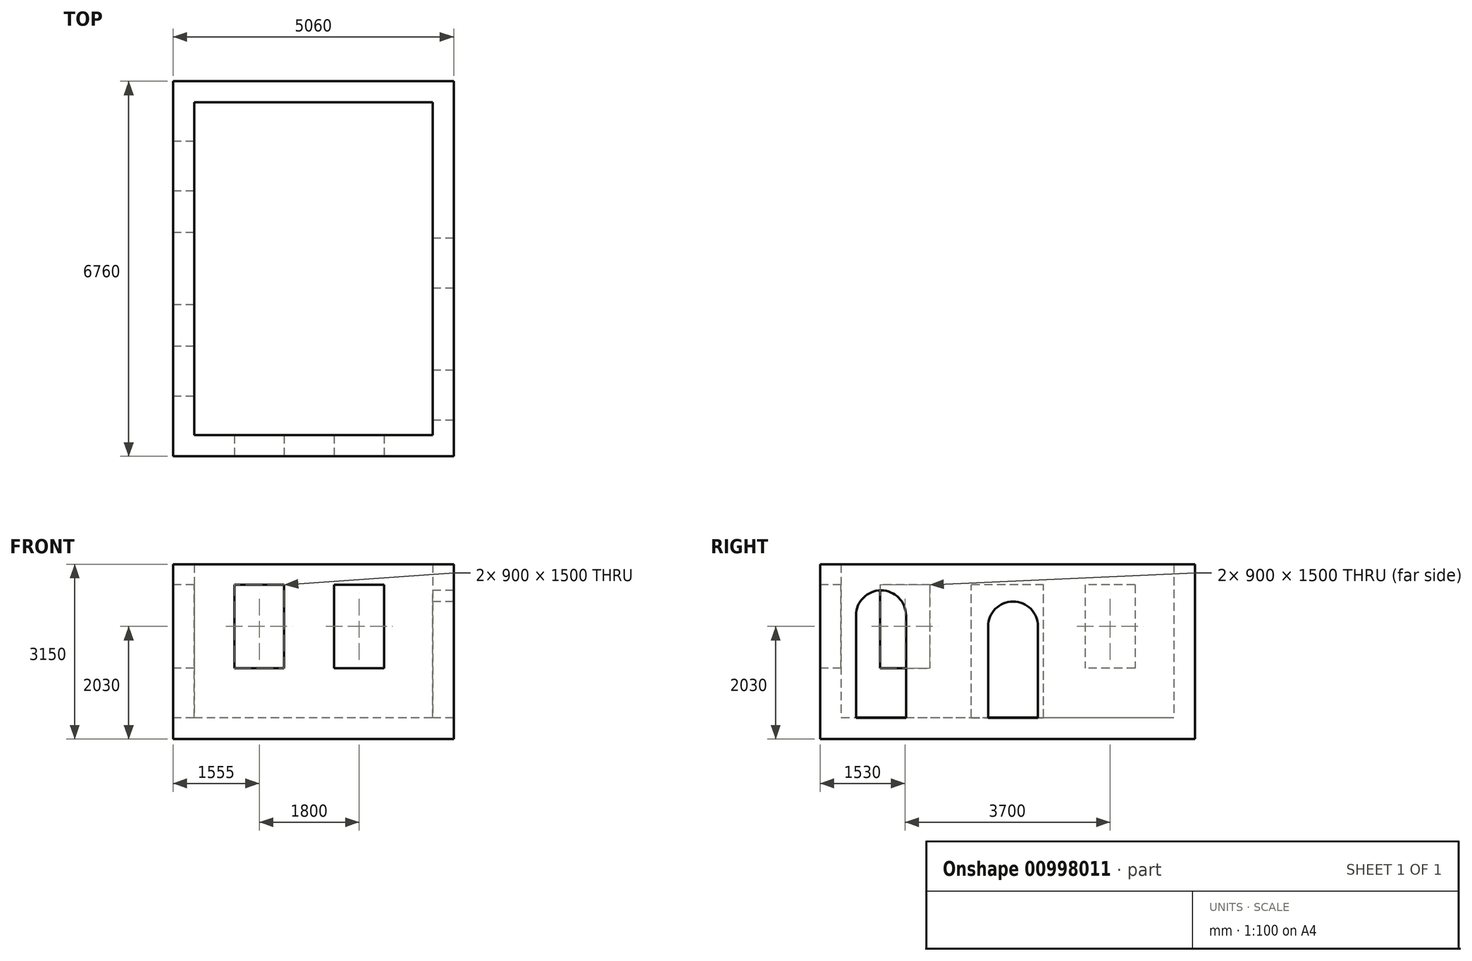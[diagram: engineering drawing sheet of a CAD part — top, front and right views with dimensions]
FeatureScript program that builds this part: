
annotation { "Feature Type Name" : "Feature", "Feature Type Description" : "" }
export const myFeature = defineFeature(function(context is Context, id is Id, definition is map)
    precondition{}
    {
        {
            var Q0;
            Q0=qCreatedBy(makeId("Top.planeOp"),FACE);
            var sketch = newSketch(context, id + "F0", { "sketchPlane" : qUnion([Q0])});
            skLineSegment(sketch, "E0.bottom", {"start": v(-2530, -3380) * mm, "end": v(2530, -3380) * mm});
            skLineSegment(sketch, "E0.top", {"start": v(-2530, 3380) * mm, "end": v(2530, 3380) * mm});
            skLineSegment(sketch, "E0.left", {"start": v(-2530, -3380) * mm, "end": v(-2530, 3380) * mm});
            skLineSegment(sketch, "E0.right", {"start": v(2530, -3380) * mm, "end": v(2530, 3380) * mm});
            skLineSegment(sketch, "E1", {"start": v(0, 0) * mm, "end": v(0, -4189.53) * mm, "construction": true});
            skLineSegment(sketch, "E2", {"start": v(59.84, 0) * mm, "end": v(5067.34, 0) * mm, "construction": true});
            skSolve(sketch);
        }
        {
            var Q0;
            Q0 = qSketchRegion(id + "F0", true);
            extrude(context, id + "F1", {"entities" : qUnion([Q0]), "depth" : (2750 + 400) * mm, "offsetDistance" : 25 * mm});
        }
        {
            var Q0;
            Q0=makeQuery(id+"F1.opExtrude","CAP_FACE",FACE,{"disambiguationData":[OSD([sQuery(id+"F0.wireOp",EDGE,"E0.bottom"),sQuery(id+"F0.wireOp",EDGE,"E0.top"),sQuery(id+"F0.wireOp",EDGE,"E0.left"),sQuery(id+"F0.wireOp",EDGE,"E0.right")])],"isStart":false});
            shell(context, id + "F2", {"entities" : qUnion([Q0]), "thickness" : 380 * mm});
        }
        {
            var Q0;
            Q0=makeQuery(id+"F1.opExtrude","SWEPT_FACE",FACE,{"disambiguationData":[OSD([sQuery(id+"F0.wireOp",EDGE,"E0.left")])]});
            var sketch = newSketch(context, id + "F3", { "sketchPlane" : qUnion([Q0])});
            skLineSegment(sketch, "E3.bottom", {"start": v(-650, 380) * mm, "end": v(650, 380) * mm});
            skLineSegment(sketch, "E3.top", {"start": v(-650, 2780) * mm, "end": v(650, 2780) * mm});
            skLineSegment(sketch, "E3.left", {"start": v(-650, 380) * mm, "end": v(-650, 2780) * mm});
            skLineSegment(sketch, "E3.right", {"start": v(650, 380) * mm, "end": v(650, 2780) * mm});
            skLineSegment(sketch, "E4", {"start": v(0, 2780) * mm, "end": v(0, 380) * mm, "construction": true});
            skLineSegment(sketch, "E5.bottom", {"start": v(-2300, 2780) * mm, "end": v(-1400, 2780) * mm});
            skLineSegment(sketch, "E5.top", {"start": v(-2300, 1280) * mm, "end": v(-1400, 1280) * mm});
            skLineSegment(sketch, "E5.left", {"start": v(-2300, 2780) * mm, "end": v(-2300, 1280) * mm});
            skLineSegment(sketch, "E5.right", {"start": v(-1400, 2780) * mm, "end": v(-1400, 1280) * mm});
            skLineSegment(sketch, "E6", {"start": v(-1850, 2780) * mm, "end": v(-1850, 1280) * mm, "construction": true});
            skLineSegment(sketch, "E7.MirrorCS", {"start": v(-1400, 2780) * mm, "end": v(-2300, 2780) * mm});
            skLineSegment(sketch, "E8.MirrorCS", {"start": v(-1400, 1280) * mm, "end": v(-2300, 1280) * mm});
            skLineSegment(sketch, "E9.MirrorCS", {"start": v(1400, 2780) * mm, "end": v(1400, 1280) * mm});
            skLineSegment(sketch, "E10.MirrorCS", {"start": v(2300, 2780) * mm, "end": v(2300, 1280) * mm});
            skLineSegment(sketch, "E11.MirrorCS", {"start": v(2300, 1280) * mm, "end": v(1400, 1280) * mm});
            skLineSegment(sketch, "E12.MirrorCS", {"start": v(1400, 2780) * mm, "end": v(2300, 2780) * mm});
            skLineSegment(sketch, "E13.MirrorCS", {"start": v(2300, 2780) * mm, "end": v(1400, 2780) * mm});
            skLineSegment(sketch, "E14.MirrorCS", {"start": v(1400, 1280) * mm, "end": v(2300, 1280) * mm});
            skLineSegment(sketch, "E15.MirrorCS", {"start": v(1850, 2780) * mm, "end": v(1850, 1280) * mm, "construction": true});
            skSolve(sketch);
        }
        {
            var Q0;
            Q0 = qSketchRegion(id + "F3", true);
            extrude(context, id + "F4", {"entities" : qUnion([Q0]), "operationType" : NewBodyOperationType.REMOVE, "oppositeDirection" : true, "depth" : 500 * mm, "offsetDistance" : 25 * mm});
        }
        {
            var Q0;
            Q0=makeQuery(id+"F1.opExtrude","SWEPT_FACE",FACE,{"disambiguationData":[OSD([sQuery(id+"F0.wireOp",EDGE,"E0.bottom")])]});
            var sketch = newSketch(context, id + "F5", { "sketchPlane" : qUnion([Q0])});
            skLineSegment(sketch, "E16.bottom", {"start": v(-1425, 2780) * mm, "end": v(-525, 2780) * mm});
            skLineSegment(sketch, "E16.top", {"start": v(-1425, 1280) * mm, "end": v(-525, 1280) * mm});
            skLineSegment(sketch, "E16.left", {"start": v(-1425, 2780) * mm, "end": v(-1425, 1280) * mm});
            skLineSegment(sketch, "E16.right", {"start": v(-525, 2780) * mm, "end": v(-525, 1280) * mm});
            skLineSegment(sketch, "E17.bottom", {"start": v(375, 2780) * mm, "end": v(1275, 2780) * mm});
            skLineSegment(sketch, "E17.top", {"start": v(375, 1280) * mm, "end": v(1275, 1280) * mm});
            skLineSegment(sketch, "E17.left", {"start": v(375, 2780) * mm, "end": v(375, 1280) * mm});
            skLineSegment(sketch, "E17.right", {"start": v(1275, 2780) * mm, "end": v(1275, 1280) * mm});
            skSolve(sketch);
        }
        {
            var Q0;
            Q0 = qSketchRegion(id + "F5", true);
            extrude(context, id + "F6", {"entities" : qUnion([Q0]), "operationType" : NewBodyOperationType.REMOVE, "oppositeDirection" : true, "depth" : 500 * mm, "offsetDistance" : 25 * mm});
        }
        {
            var Q0;
            Q0=makeQuery(id+"F2.opShell","OFFSET_FACE",FACE,{"disambiguationData":[OSD([sQuery(id+"F0.wireOp",EDGE,"E0.right")])]});
            var sketch = newSketch(context, id + "F7", { "sketchPlane" : qUnion([Q0])});
            skLineSegment(sketch, "E18.bottom", {"start": v(-550, 380) * mm, "end": v(350, 380) * mm});
            skLineSegment(sketch, "E18.left", {"start": v(-550, 380) * mm, "end": v(-550, 2030) * mm});
            skLineSegment(sketch, "E18.right", {"start": v(350, 380) * mm, "end": v(350, 2030) * mm});
            skArc(sketch, "E19", {"start": v(350, 2030) * mm, "mid": v(-100, 2480) * mm, "end": v(-550, 2030) * mm});
            skLineSegment(sketch, "E20.bottom", {"start": v(1830, 380) * mm, "end": v(2730, 380) * mm});
            skLineSegment(sketch, "E20.left", {"start": v(1830, 380) * mm, "end": v(1830, 2230) * mm});
            skLineSegment(sketch, "E20.right", {"start": v(2730, 380) * mm, "end": v(2730, 2230) * mm});
            skArc(sketch, "E21", {"start": v(2730, 2230) * mm, "mid": v(2280, 2680) * mm, "end": v(1830, 2230) * mm});
            skSolve(sketch);
        }
        {
            var Q0;
            Q0 = qSketchRegion(id + "F7", true);
            extrude(context, id + "F8", {"entities" : qUnion([Q0]), "operationType" : NewBodyOperationType.REMOVE, "endBound" : BoundingType.THROUGH_ALL, "oppositeDirection" : true, "depth" : 25 * mm, "offsetDistance" : 25 * mm});
        }
        {
            var Q0;
            Q0=makeQuery(id+"F8.boolean.opBoolean","MERGE",FACE,{"derivedFrom":[makeQuery(id+"F4.boolean.opBoolean","MERGE",FACE,{"derivedFrom":[makeQuery(id+"F2.opShell","OFFSET_FACE",FACE,{"disambiguationData":[OSD([sQuery(id+"F0.wireOp",EDGE,"E0.bottom"),sQuery(id+"F0.wireOp",EDGE,"E0.top"),sQuery(id+"F0.wireOp",EDGE,"E0.left"),sQuery(id+"F0.wireOp",EDGE,"E0.right")])]})],"fromTools":[makeQuery(id+"F4.opExtrude","SWEPT_FACE",FACE,{"disambiguationData":[OSD([sQuery(id+"F3.wireOp",EDGE,"E3.bottom")])]})]})],"fromTools":[makeQuery(id+"F8.opExtrude","SWEPT_FACE",FACE,{"disambiguationData":[OSD([sQuery(id+"F7.wireOp",EDGE,"E18.bottom")])]}),makeQuery(id+"F8.opExtrude","SWEPT_FACE",FACE,{"disambiguationData":[OSD([sQuery(id+"F7.wireOp",EDGE,"E20.bottom")])]})]});
            var sketch = newSketch(context, id + "F9", { "sketchPlane" : qUnion([Q0])});
            skLineSegment(sketch, "E22.bottom", {"start": v(-2150, 3000) * mm, "end": v(2150, 3000) * mm});
            skLineSegment(sketch, "E22.top", {"start": v(-2150, -3000) * mm, "end": v(2150, -3000) * mm});
            skLineSegment(sketch, "E22.left", {"start": v(-2150, 3000) * mm, "end": v(-2150, -3000) * mm});
            skLineSegment(sketch, "E22.right", {"start": v(2150, 3000) * mm, "end": v(2150, -3000) * mm});
            skSolve(sketch);
        }
        {
            var Q0;
            Q0 = qSketchRegion(id + "F9", true);
            extrude(context, id + "F10", {"entities" : qUnion([Q0]), "operationType" : NewBodyOperationType.ADD, "depth" : 8 * mm, "offsetDistance" : 25 * mm});
        }
    });
